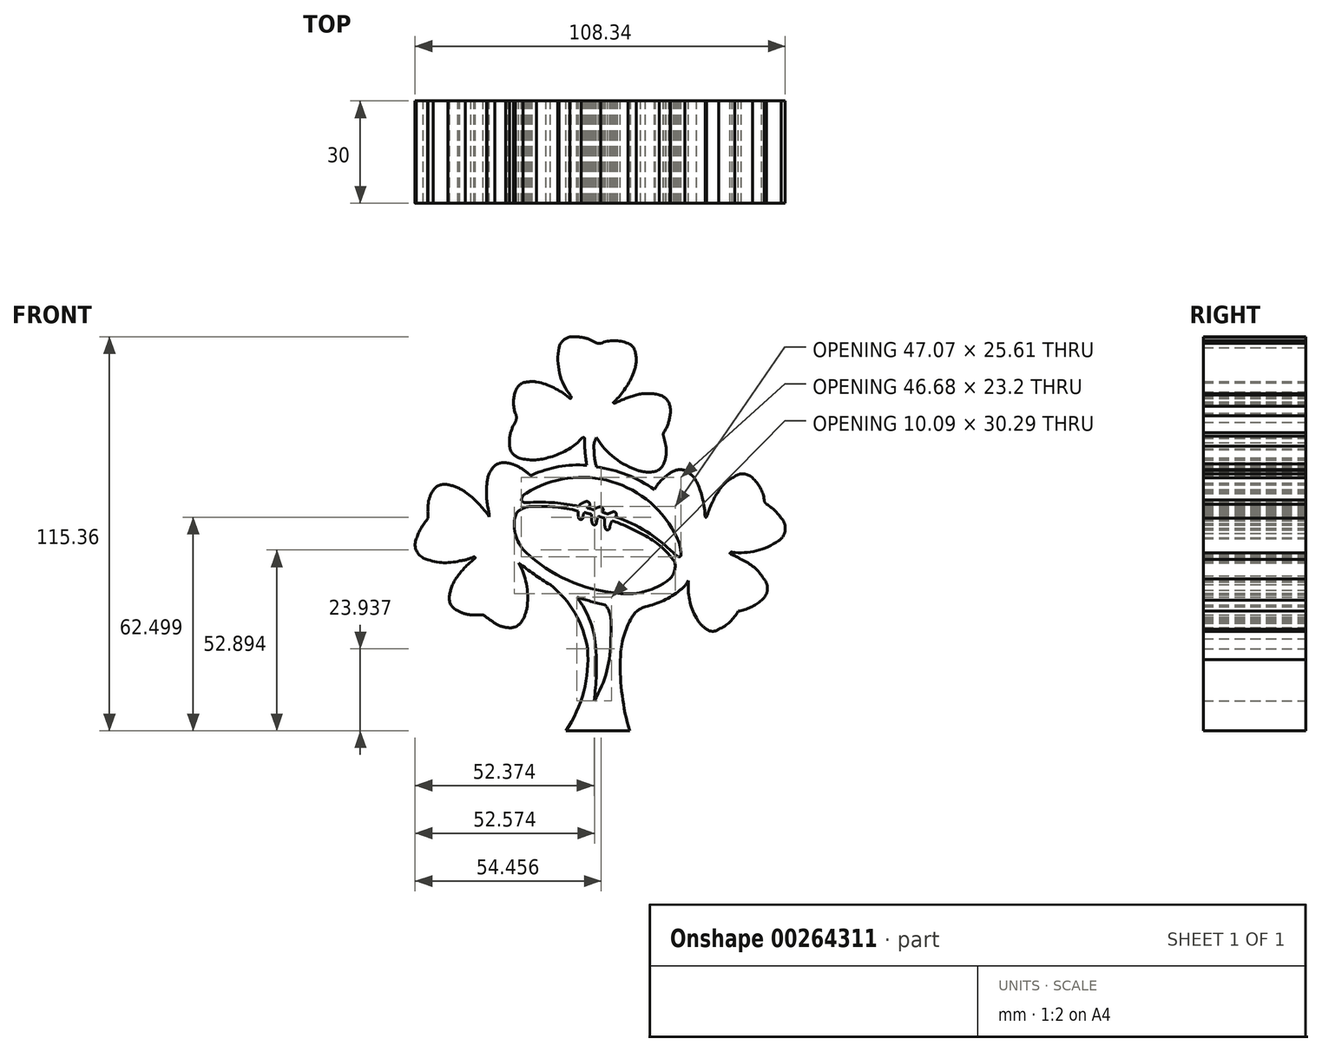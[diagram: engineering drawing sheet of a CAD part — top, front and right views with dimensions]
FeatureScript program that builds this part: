
annotation { "Feature Type Name" : "Feature", "Feature Type Description" : "" }
export const myFeature = defineFeature(function(context is Context, id is Id, definition is map)
    precondition{}
    {
        {
            var Q0;
            Q0=qCreatedBy(makeId("Front.planeOp"),FACE);
            var sketch = newSketch(context, id + "F0", { "sketchPlane" : qUnion([Q0])});
            skLineSegment(sketch, "E0", {"start": v(-7.06, -41.09) * mm, "end": v(11.5, -41.09) * mm});
            skArc(sketch, "E1", {"start": v(8.82, -20.29) * mm, "mid": v(9.34, -30.8) * mm, "end": v(11.5, -41.09) * mm});
            skArc(sketch, "E2", {"start": v(11.79, -8.6) * mm, "mid": v(9.58, -14.26) * mm, "end": v(8.82, -20.29) * mm});
            skArc(sketch, "E3", {"start": v(16.1, -4.74) * mm, "mid": v(13.54, -6.22) * mm, "end": v(11.79, -8.6) * mm});
            skArc(sketch, "E4", {"start": v(16.1, -4.74) * mm, "mid": v(21.44, -2.99) * mm, "end": v(26.21, 0) * mm});
            skArc(sketch, "E5", {"start": v(26.21, 0) * mm, "mid": v(27.64, 1.28) * mm, "end": v(28.73, 2.86) * mm});
            skArc(sketch, "E6", {"start": v(28.73, 2.86) * mm, "mid": v(29.05, -2.8) * mm, "end": v(31.08, -8.1) * mm});
            skArc(sketch, "E7", {"start": v(31.08, -8.1) * mm, "mid": v(32.36, -9.96) * mm, "end": v(34.1, -11.4) * mm});
            skArc(sketch, "E8", {"start": v(34.1, -11.4) * mm, "mid": v(35.83, -12) * mm, "end": v(37.56, -11.4) * mm});
            skArc(sketch, "E9", {"start": v(37.56, -11.4) * mm, "mid": v(40.87, -9.22) * mm, "end": v(43.27, -6.08) * mm});
            skArc(sketch, "E10", {"start": v(43.27, -6.08) * mm, "mid": v(46.94, -4.95) * mm, "end": v(50.15, -2.84) * mm});
            skArc(sketch, "E11", {"start": v(50.15, -2.84) * mm, "mid": v(51.83, 0.14) * mm, "end": v(50.78, 3.4) * mm});
            skArc(sketch, "E12", {"start": v(50.78, 3.4) * mm, "mid": v(47.96, 6.71) * mm, "end": v(44.26, 9.01) * mm});
            skArc(sketch, "E13", {"start": v(44.26, 9.01) * mm, "mid": v(42.77, 9.87) * mm, "end": v(41.18, 10.53) * mm});
            skArc(sketch, "E14", {"start": v(41.5, 11.13) * mm, "mid": v(40.99, 11.03) * mm, "end": v(41.18, 10.53) * mm});
            skArc(sketch, "E15", {"start": v(41.5, 11.13) * mm, "mid": v(48.65, 11.6) * mm, "end": v(55.17, 14.55) * mm});
            skArc(sketch, "E16", {"start": v(55.17, 14.55) * mm, "mid": v(57.05, 17.68) * mm, "end": v(55.9, 21.14) * mm});
            skArc(sketch, "E17", {"start": v(55.9, 21.14) * mm, "mid": v(53.95, 23.38) * mm, "end": v(51.62, 25.23) * mm});
            skArc(sketch, "E18", {"start": v(50.92, 26.52) * mm, "mid": v(51.1, 25.78) * mm, "end": v(51.62, 25.23) * mm});
            skArc(sketch, "E19", {"start": v(50.92, 26.52) * mm, "mid": v(49.76, 30.02) * mm, "end": v(47.46, 32.9) * mm});
            skArc(sketch, "E20", {"start": v(47.46, 32.9) * mm, "mid": v(44.93, 34.1) * mm, "end": v(42.24, 33.3) * mm});
            skArc(sketch, "E21", {"start": v(42.24, 33.3) * mm, "mid": v(39.6, 31.52) * mm, "end": v(37.57, 29.06) * mm});
            skArc(sketch, "E22", {"start": v(37.57, 29.06) * mm, "mid": v(35.57, 25.44) * mm, "end": v(34.09, 21.59) * mm});
            skArc(sketch, "E23", {"start": v(33.61, 21.59) * mm, "mid": v(33.85, 21.4) * mm, "end": v(34.09, 21.59) * mm});
            skArc(sketch, "E24", {"start": v(33.61, 21.59) * mm, "mid": v(32.95, 26.57) * mm, "end": v(31.35, 31.34) * mm});
            skArc(sketch, "E25", {"start": v(31.35, 31.34) * mm, "mid": v(29.86, 33.56) * mm, "end": v(27.7, 35.12) * mm});
            skArc(sketch, "E26", {"start": v(27.7, 35.12) * mm, "mid": v(25.19, 35.2) * mm, "end": v(22.97, 34.03) * mm});
            skArc(sketch, "E27", {"start": v(22.97, 34.03) * mm, "mid": v(20.6, 32) * mm, "end": v(18.78, 29.47) * mm});
            skArc(sketch, "E28", {"start": v(18.78, 29.47) * mm, "mid": v(10.7, 33.83) * mm, "end": v(1.8, 36.17) * mm});
            skArc(sketch, "E29", {"start": v(1.1, 41.24) * mm, "mid": v(1.26, 38.68) * mm, "end": v(1.8, 36.17) * mm});
            skArc(sketch, "E30", {"start": v(1.8, 44.73) * mm, "mid": v(1.13, 43.05) * mm, "end": v(1.1, 41.24) * mm});
            skArc(sketch, "E31", {"start": v(1.8, 44.73) * mm, "mid": v(7.14, 38.73) * mm, "end": v(14.27, 35.03) * mm});
            skArc(sketch, "E32", {"start": v(14.27, 35.03) * mm, "mid": v(16.62, 34.62) * mm, "end": v(19, 34.8) * mm});
            skArc(sketch, "E33", {"start": v(19, 34.8) * mm, "mid": v(20.5, 35.63) * mm, "end": v(21.46, 37.04) * mm});
            skArc(sketch, "E34", {"start": v(21.46, 37.04) * mm, "mid": v(22.19, 39.6) * mm, "end": v(22.16, 42.24) * mm});
            skArc(sketch, "E35", {"start": v(21.46, 45.07) * mm, "mid": v(21.79, 43.65) * mm, "end": v(22.16, 42.24) * mm});
            skArc(sketch, "E36", {"start": v(21.46, 46.14) * mm, "mid": v(21.37, 45.6) * mm, "end": v(21.46, 45.07) * mm});
            skArc(sketch, "E37", {"start": v(21.46, 46.14) * mm, "mid": v(22.7, 48.53) * mm, "end": v(23.35, 51.13) * mm});
            skArc(sketch, "E38", {"start": v(23.35, 51.13) * mm, "mid": v(23.48, 52.5) * mm, "end": v(23.35, 53.88) * mm});
            skArc(sketch, "E39", {"start": v(23.35, 53.88) * mm, "mid": v(22.22, 56) * mm, "end": v(20.17, 57.22) * mm});
            skArc(sketch, "E40", {"start": v(20.17, 57.22) * mm, "mid": v(16.84, 57.62) * mm, "end": v(13.52, 57.22) * mm});
            skArc(sketch, "E41", {"start": v(13.52, 57.22) * mm, "mid": v(10.25, 56.13) * mm, "end": v(7.1, 54.73) * mm});
            skArc(sketch, "E42", {"start": v(6.96, 55.22) * mm, "mid": v(6.79, 54.9) * mm, "end": v(7.1, 54.73) * mm});
            skArc(sketch, "E43", {"start": v(6.96, 55.22) * mm, "mid": v(10.33, 59.18) * mm, "end": v(12.72, 63.8) * mm});
            skArc(sketch, "E44", {"start": v(12.72, 63.8) * mm, "mid": v(13.4, 66.76) * mm, "end": v(13.18, 69.8) * mm});
            skArc(sketch, "E45", {"start": v(13.18, 69.8) * mm, "mid": v(12.42, 71.33) * mm, "end": v(11.02, 72.32) * mm});
            skArc(sketch, "E46", {"start": v(11.02, 72.32) * mm, "mid": v(7.02, 73.1) * mm, "end": v(3.03, 72.32) * mm});
            skArc(sketch, "E47", {"start": v(1.55, 72.55) * mm, "mid": v(2.26, 72.27) * mm, "end": v(3.03, 72.32) * mm});
            skArc(sketch, "E48", {"start": v(1.55, 72.55) * mm, "mid": v(-0.46, 73.56) * mm, "end": v(-2.65, 74.07) * mm});
            skArc(sketch, "E49", {"start": v(-2.65, 74.07) * mm, "mid": v(-4.32, 74.27) * mm, "end": v(-6, 74.15) * mm});
            skArc(sketch, "E50", {"start": v(-6, 74.15) * mm, "mid": v(-8, 73.07) * mm, "end": v(-9.13, 71.1) * mm});
            skArc(sketch, "E51", {"start": v(-9.13, 71.1) * mm, "mid": v(-8.99, 63.61) * mm, "end": v(-5.69, 56.9) * mm});
            skArc(sketch, "E52", {"start": v(-5.55, 56.29) * mm, "mid": v(-5.57, 56.6) * mm, "end": v(-5.69, 56.9) * mm});
            skArc(sketch, "E53", {"start": v(-6.27, 56.43) * mm, "mid": v(-5.94, 56.22) * mm, "end": v(-5.55, 56.29) * mm});
            skArc(sketch, "E54", {"start": v(-6.27, 56.43) * mm, "mid": v(-10.7, 59.33) * mm, "end": v(-15.7, 61.03) * mm});
            skArc(sketch, "E55", {"start": v(-15.7, 61.03) * mm, "mid": v(-17.69, 61.07) * mm, "end": v(-19.66, 60.77) * mm});
            skArc(sketch, "E56", {"start": v(-19.66, 60.77) * mm, "mid": v(-21.1, 59.7) * mm, "end": v(-21.94, 58.13) * mm});
            skArc(sketch, "E57", {"start": v(-21.94, 58.13) * mm, "mid": v(-22.49, 55.02) * mm, "end": v(-21.94, 51.9) * mm});
            skArc(sketch, "E58", {"start": v(-21.94, 49.26) * mm, "mid": v(-21.62, 50.58) * mm, "end": v(-21.94, 51.9) * mm});
            skArc(sketch, "E59", {"start": v(-21.94, 49.26) * mm, "mid": v(-23.03, 46.99) * mm, "end": v(-23.63, 44.54) * mm});
            skArc(sketch, "E60", {"start": v(-23.63, 44.54) * mm, "mid": v(-23.66, 43) * mm, "end": v(-23.48, 41.48) * mm});
            skArc(sketch, "E61", {"start": v(-23.48, 41.48) * mm, "mid": v(-22.55, 39.87) * mm, "end": v(-21, 38.84) * mm});
            skArc(sketch, "E62", {"start": v(-21, 38.84) * mm, "mid": v(-17, 38.16) * mm, "end": v(-12.97, 38.7) * mm});
            skArc(sketch, "E63", {"start": v(-12.97, 38.7) * mm, "mid": v(-8.04, 40.4) * mm, "end": v(-3.65, 43.21) * mm});
            skArc(sketch, "E64", {"start": v(-2.2, 44.74) * mm, "mid": v(-3, 44.04) * mm, "end": v(-3.65, 43.21) * mm});
            skArc(sketch, "E65", {"start": v(-1.65, 44.54) * mm, "mid": v(-1.88, 44.77) * mm, "end": v(-2.2, 44.74) * mm});
            skArc(sketch, "E66", {"start": v(-1.65, 44.54) * mm, "mid": v(-1.53, 40.55) * mm, "end": v(-1.04, 36.6) * mm});
            skArc(sketch, "E67", {"start": v(-1.04, 36.6) * mm, "mid": v(-9.25, 36.2) * mm, "end": v(-17.09, 33.73) * mm});
            skArc(sketch, "E68", {"start": v(-17.98, 33.98) * mm, "mid": v(-17.56, 33.76) * mm, "end": v(-17.09, 33.73) * mm});
            skArc(sketch, "E69", {"start": v(-17.98, 33.98) * mm, "mid": v(-19.98, 35.55) * mm, "end": v(-22.22, 36.77) * mm});
            skArc(sketch, "E70", {"start": v(-22.22, 36.77) * mm, "mid": v(-23.45, 37.14) * mm, "end": v(-24.7, 37.35) * mm});
            skArc(sketch, "E71", {"start": v(-24.7, 37.35) * mm, "mid": v(-26.43, 37.26) * mm, "end": v(-27.95, 36.46) * mm});
            skArc(sketch, "E72", {"start": v(-27.95, 36.46) * mm, "mid": v(-29.58, 34.2) * mm, "end": v(-30.2, 31.47) * mm});
            skArc(sketch, "E73", {"start": v(-30.2, 31.47) * mm, "mid": v(-30.38, 27.65) * mm, "end": v(-29.87, 23.87) * mm});
            skArc(sketch, "E74", {"start": v(-29.54, 21.48) * mm, "mid": v(-29.64, 22.68) * mm, "end": v(-29.87, 23.87) * mm});
            skArc(sketch, "E75", {"start": v(-29.54, 21.48) * mm, "mid": v(-32.73, 25.42) * mm, "end": v(-36.54, 28.78) * mm});
            skArc(sketch, "E76", {"start": v(-36.54, 28.78) * mm, "mid": v(-39, 30.13) * mm, "end": v(-41.68, 30.93) * mm});
            skArc(sketch, "E77", {"start": v(-41.68, 30.93) * mm, "mid": v(-44.12, 30.78) * mm, "end": v(-46, 29.2) * mm});
            skArc(sketch, "E78", {"start": v(-46, 29.2) * mm, "mid": v(-47.01, 27.24) * mm, "end": v(-47.45, 25.06) * mm});
            skArc(sketch, "E79", {"start": v(-47.45, 25.06) * mm, "mid": v(-47.56, 23.07) * mm, "end": v(-47.45, 21.08) * mm});
            skArc(sketch, "E80", {"start": v(-47.45, 21.08) * mm, "mid": v(-49.44, 18.3) * mm, "end": v(-50.88, 15.19) * mm});
            skArc(sketch, "E81", {"start": v(-50.88, 15.19) * mm, "mid": v(-51, 11.92) * mm, "end": v(-48.83, 9.47) * mm});
            skArc(sketch, "E82", {"start": v(-48.83, 9.47) * mm, "mid": v(-43.58, 8.14) * mm, "end": v(-38.18, 8.64) * mm});
            skArc(sketch, "E83", {"start": v(-38.18, 8.64) * mm, "mid": v(-36.08, 9.07) * mm, "end": v(-34.06, 9.82) * mm});
            skArc(sketch, "E84", {"start": v(-33.8, 9.29) * mm, "mid": v(-33.72, 9.65) * mm, "end": v(-34.06, 9.82) * mm});
            skArc(sketch, "E85", {"start": v(-33.8, 9.29) * mm, "mid": v(-36.48, 6.92) * mm, "end": v(-38.79, 4.2) * mm});
            skArc(sketch, "E86", {"start": v(-38.79, 4.2) * mm, "mid": v(-40.33, 1.54) * mm, "end": v(-41.2, -1.4) * mm});
            skArc(sketch, "E87", {"start": v(-41.2, -1.4) * mm, "mid": v(-40.83, -4.12) * mm, "end": v(-38.79, -5.96) * mm});
            skArc(sketch, "E88", {"start": v(-38.79, -5.96) * mm, "mid": v(-36.93, -6.78) * mm, "end": v(-34.94, -7.16) * mm});
            skArc(sketch, "E89", {"start": v(-34.94, -7.16) * mm, "mid": v(-33.16, -7.2) * mm, "end": v(-31.37, -7.16) * mm});
            skArc(sketch, "E90", {"start": v(-27.95, -9.6) * mm, "mid": v(-29.66, -8.38) * mm, "end": v(-31.37, -7.16) * mm});
            skArc(sketch, "E91", {"start": v(-27.95, -9.6) * mm, "mid": v(-26.07, -10.53) * mm, "end": v(-24, -10.91) * mm});
            skArc(sketch, "E92", {"start": v(-24, -10.91) * mm, "mid": v(-21.77, -10.6) * mm, "end": v(-20.07, -9.13) * mm});
            skArc(sketch, "E93", {"start": v(-20.07, -9.13) * mm, "mid": v(-19.02, -6.91) * mm, "end": v(-18.42, -4.53) * mm});
            skArc(sketch, "E94", {"start": v(-18.42, -4.53) * mm, "mid": v(-18.7, 1.92) * mm, "end": v(-20.9, 7.99) * mm});
            skArc(sketch, "E95", {"start": v(-20.9, 7.99) * mm, "mid": v(-16.4, 4.68) * mm, "end": v(-11.7, 1.64) * mm});
            skArc(sketch, "E96", {"start": v(-0.8, -17.1) * mm, "mid": v(-4.46, -6.69) * mm, "end": v(-11.7, 1.64) * mm});
            skArc(sketch, "E97", {"start": v(-7.06, -41.09) * mm, "mid": v(-1.92, -29.62) * mm, "end": v(-0.8, -17.1) * mm});
            skArc(sketch, "E98", {"start": v(1.13, -32.3) * mm, "mid": v(4.85, -23.57) * mm, "end": v(5.98, -14.15) * mm});
            skArc(sketch, "E99", {"start": v(5.98, -14.15) * mm, "mid": v(6.16, -11) * mm, "end": v(5.98, -7.84) * mm});
            skArc(sketch, "E100", {"start": v(5.98, -7.84) * mm, "mid": v(5.42, -5.91) * mm, "end": v(4.29, -4.25) * mm});
            skArc(sketch, "E101", {"start": v(-3.93, -2) * mm, "mid": v(0.16, -3.2) * mm, "end": v(4.29, -4.25) * mm});
            skArc(sketch, "E102", {"start": v(1.6, -17.1) * mm, "mid": v(0, -9.13) * mm, "end": v(-3.93, -2) * mm});
            skArc(sketch, "E103", {"start": v(1.13, -32.3) * mm, "mid": v(1.76, -24.71) * mm, "end": v(1.6, -17.1) * mm});
            skArc(sketch, "E104", {"start": v(-21.65, 22.6) * mm, "mid": v(-21.94, 16.54) * mm, "end": v(-18.97, 11.24) * mm});
            skArc(sketch, "E105", {"start": v(-18.97, 11.24) * mm, "mid": v(-6.5, 2.92) * mm, "end": v(8.02, -0.83) * mm});
            skArc(sketch, "E106", {"start": v(8.02, -0.83) * mm, "mid": v(15.35, -0.48) * mm, "end": v(22.06, 2.48) * mm});
            skArc(sketch, "E107", {"start": v(22.06, 2.48) * mm, "mid": v(24.36, 4.92) * mm, "end": v(24.74, 8.24) * mm});
            skArc(sketch, "E108", {"start": v(6.36, 20.4) * mm, "mid": v(5.93, 19.33) * mm, "end": v(5.68, 18.21) * mm});
            skArc(sketch, "E109", {"start": v(4.4, 18.21) * mm, "mid": v(5.04, 17.67) * mm, "end": v(5.68, 18.21) * mm});
            skArc(sketch, "E110", {"start": v(4.26, 21.1) * mm, "mid": v(4.15, 19.64) * mm, "end": v(4.4, 18.21) * mm});
            skArc(sketch, "E111", {"start": v(2.4, 21.68) * mm, "mid": v(3.34, 21.38) * mm, "end": v(4.26, 21.1) * mm});
            skArc(sketch, "E112", {"start": v(2.4, 21.68) * mm, "mid": v(1.97, 20.68) * mm, "end": v(1.84, 19.6) * mm});
            skArc(sketch, "E113", {"start": v(0.6, 19.6) * mm, "mid": v(1.22, 19.14) * mm, "end": v(1.84, 19.6) * mm});
            skArc(sketch, "E114", {"start": v(0.39, 22.3) * mm, "mid": v(0.33, 20.94) * mm, "end": v(0.6, 19.6) * mm});
            skArc(sketch, "E115", {"start": v(-1.7, 22.8) * mm, "mid": v(-0.67, 22.5) * mm, "end": v(0.39, 22.3) * mm});
            skArc(sketch, "E116", {"start": v(-1.7, 22.8) * mm, "mid": v(-2.04, 22.05) * mm, "end": v(-2.13, 21.23) * mm});
            skArc(sketch, "E117", {"start": v(-3.42, 21.23) * mm, "mid": v(-2.77, 20.7) * mm, "end": v(-2.13, 21.23) * mm});
            skArc(sketch, "E118", {"start": v(-3.62, 23.22) * mm, "mid": v(-3.55, 22.22) * mm, "end": v(-3.42, 21.23) * mm});
            skArc(sketch, "E119", {"start": v(-3.62, 23.22) * mm, "mid": v(-10.23, 24.4) * mm, "end": v(-16.95, 24.55) * mm});
            skArc(sketch, "E120", {"start": v(-16.95, 24.55) * mm, "mid": v(-19.5, 24.07) * mm, "end": v(-21.65, 22.6) * mm});
            skArc(sketch, "E121", {"start": v(-18.78, 28.42) * mm, "mid": v(-19.77, 27.57) * mm, "end": v(-20.15, 26.33) * mm});
            skArc(sketch, "E122", {"start": v(-3.42, 24.55) * mm, "mid": v(-10.4, 25.65) * mm, "end": v(-17.48, 25.74) * mm});
            skArc(sketch, "E123", {"start": v(-19.34, 25.74) * mm, "mid": v(-18.41, 25.64) * mm, "end": v(-17.48, 25.74) * mm});
            skArc(sketch, "E124", {"start": v(-20.15, 26.33) * mm, "mid": v(-19.79, 25.97) * mm, "end": v(-19.34, 25.74) * mm});
            skArc(sketch, "E125", {"start": v(-1.33, 25.97) * mm, "mid": v(-2.5, 25.46) * mm, "end": v(-3.42, 24.55) * mm});
            skArc(sketch, "E126", {"start": v(-0.2, 24.8) * mm, "mid": v(-0.4, 25.76) * mm, "end": v(-1.33, 25.97) * mm});
            skArc(sketch, "E127", {"start": v(-0.9, 24.1) * mm, "mid": v(-0.52, 24.42) * mm, "end": v(-0.2, 24.8) * mm});
            skArc(sketch, "E128", {"start": v(1.01, 23.55) * mm, "mid": v(0.07, 23.88) * mm, "end": v(-0.9, 24.1) * mm});
            skArc(sketch, "E129", {"start": v(2.57, 24.37) * mm, "mid": v(1.74, 24.06) * mm, "end": v(1.01, 23.55) * mm});
            skArc(sketch, "E130", {"start": v(3.78, 23.55) * mm, "mid": v(3.42, 24.32) * mm, "end": v(2.57, 24.37) * mm});
            skArc(sketch, "E131", {"start": v(3.48, 22.95) * mm, "mid": v(3.68, 23.22) * mm, "end": v(3.78, 23.55) * mm});
            skArc(sketch, "E132", {"start": v(3.48, 22.95) * mm, "mid": v(4.29, 22.62) * mm, "end": v(5.12, 22.34) * mm});
            skArc(sketch, "E133", {"start": v(6.6, 22.95) * mm, "mid": v(5.85, 22.67) * mm, "end": v(5.12, 22.34) * mm});
            skArc(sketch, "E134", {"start": v(7.62, 22.1) * mm, "mid": v(7.35, 22.82) * mm, "end": v(6.6, 22.95) * mm});
            skArc(sketch, "E135", {"start": v(7.39, 21.57) * mm, "mid": v(7.58, 21.8) * mm, "end": v(7.62, 22.1) * mm});
            skArc(sketch, "E136", {"start": v(24.33, 10.92) * mm, "mid": v(16.46, 17.2) * mm, "end": v(7.39, 21.57) * mm});
            skArc(sketch, "E137", {"start": v(24.33, 10.92) * mm, "mid": v(25.06, 10.3) * mm, "end": v(25.9, 9.83) * mm});
            skArc(sketch, "E138", {"start": v(25.9, 9.83) * mm, "mid": v(26.36, 9.91) * mm, "end": v(26.54, 10.33) * mm});
            skArc(sketch, "E139", {"start": v(26.54, 10.33) * mm, "mid": v(26.26, 12.92) * mm, "end": v(25.41, 15.37) * mm});
            skArc(sketch, "E140", {"start": v(25.41, 15.37) * mm, "mid": v(6.25, 31.84) * mm, "end": v(-18.78, 28.42) * mm});
            skArc(sketch, "E141", {"start": v(24.74, 8.24) * mm, "mid": v(20.3, 13.1) * mm, "end": v(14.73, 16.63) * mm});
            skArc(sketch, "E142", {"start": v(14.73, 16.63) * mm, "mid": v(10.64, 18.72) * mm, "end": v(6.36, 20.4) * mm});
            skSolve(sketch);
        }
        {
            var Q0;
            Q0 = qSketchRegion(id + "F0", true);
            extrude(context, id + "F1", {"entities" : qUnion([Q0]), "depth" : 30 * mm, "offsetDistance" : 25 * mm});
        }
    });
